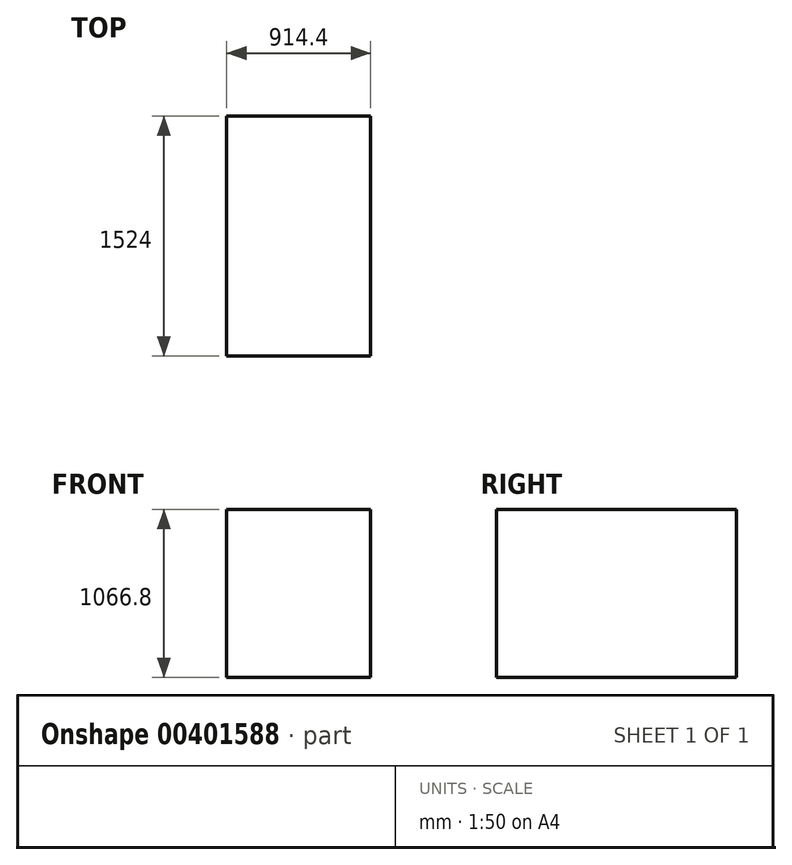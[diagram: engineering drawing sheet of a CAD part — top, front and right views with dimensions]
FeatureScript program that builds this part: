
annotation { "Feature Type Name" : "Feature", "Feature Type Description" : "" }
export const myFeature = defineFeature(function(context is Context, id is Id, definition is map)
    precondition{}
    {
        {
            var Q0;
            Q0=qCreatedBy(makeId("Front.planeOp"),FACE);
            var sketch = newSketch(context, id + "F0", { "sketchPlane" : qUnion([Q0])});
            skLineSegment(sketch, "E0.bottom", {"start": v(-457.2, 0) * mm, "end": v(457.2, 0) * mm});
            skLineSegment(sketch, "E0.top", {"start": v(-457.2, 1066.8) * mm, "end": v(457.2, 1066.8) * mm});
            skLineSegment(sketch, "E0.left", {"start": v(-457.2, 0) * mm, "end": v(-457.2, 1066.8) * mm});
            skLineSegment(sketch, "E0.right", {"start": v(457.2, 0) * mm, "end": v(457.2, 1066.8) * mm});
            skSolve(sketch);
        }
        {
            var Q0;
            Q0 = qSketchRegion(id + "F0", true);
            extrude(context, id + "F1", {"entities" : qUnion([Q0]), "oppositeDirection" : true, "depth" : 1524 * mm});
        }
    });
